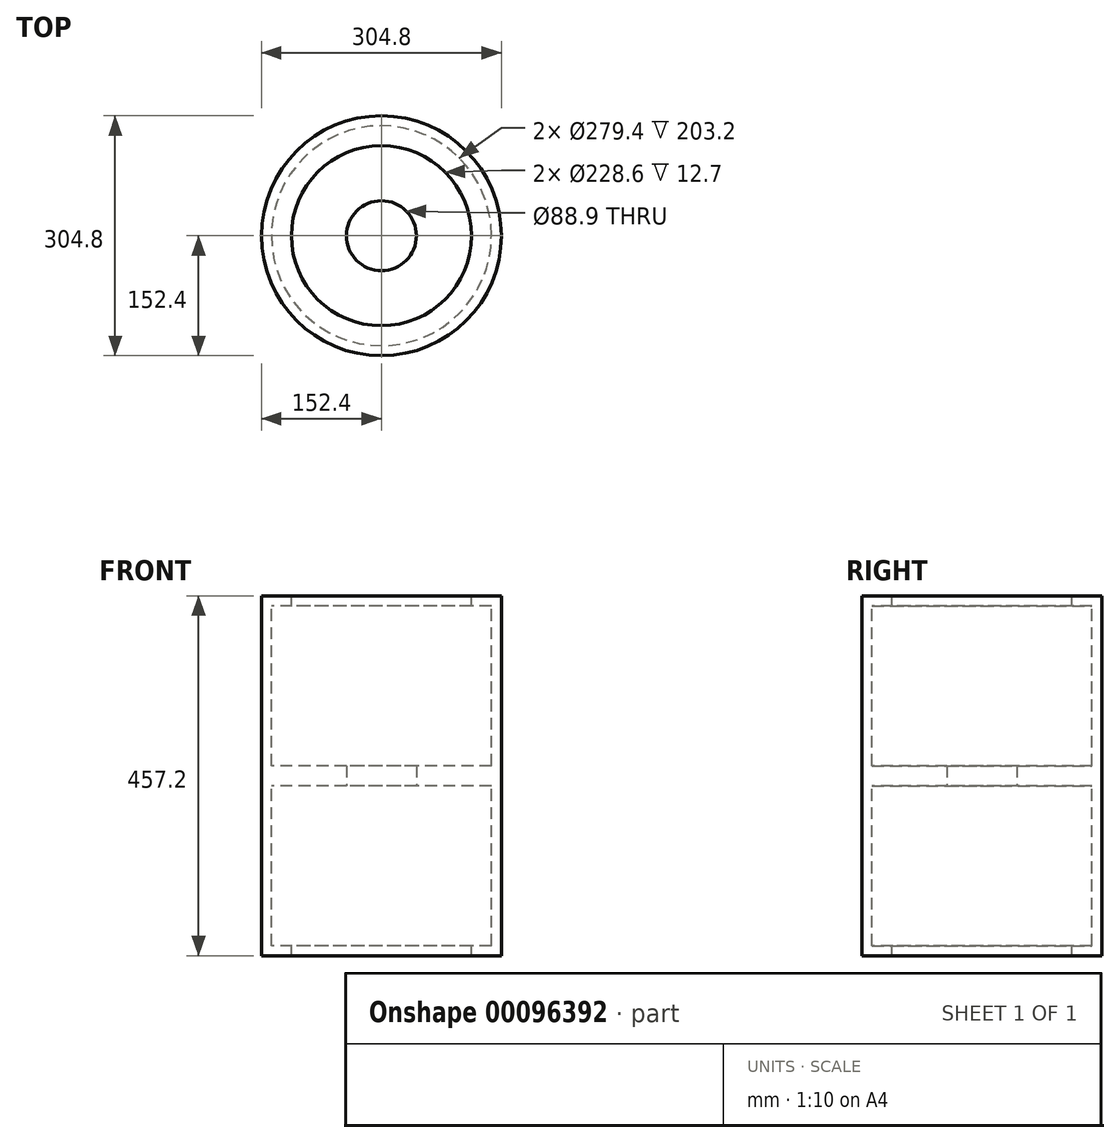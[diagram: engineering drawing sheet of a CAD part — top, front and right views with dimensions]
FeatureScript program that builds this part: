
annotation { "Feature Type Name" : "Feature", "Feature Type Description" : "" }
export const myFeature = defineFeature(function(context is Context, id is Id, definition is map)
    precondition{}
    {
        {
            var Q0;
            Q0=qCreatedBy(makeId("Front.planeOp"),FACE);
            var sketch = newSketch(context, id + "F0", { "sketchPlane" : qUnion([Q0])});
            skLineSegment(sketch, "E0.bottom", {"start": v(152.4, 228.6) * mm, "end": v(-152.4, 228.6) * mm});
            skLineSegment(sketch, "E0.top", {"start": v(152.4, -228.6) * mm, "end": v(-152.4, -228.6) * mm});
            skLineSegment(sketch, "E0.left", {"start": v(152.4, 228.6) * mm, "end": v(152.4, -228.6) * mm});
            skLineSegment(sketch, "E0.right", {"start": v(-152.4, 228.6) * mm, "end": v(-152.4, -228.6) * mm});
            skPoint(sketch, "E0.middle", {"position": v(0, 0) * mm});
            skLineSegment(sketch, "E1", {"start": v(0, 228.6) * mm, "end": v(0, -228.6) * mm});
            skLineSegment(sketch, "E2.bottom", {"start": v(114.3, 228.6) * mm, "end": v(-114.3, 228.6) * mm});
            skLineSegment(sketch, "E2.top", {"start": v(114.3, -228.6) * mm, "end": v(-114.3, -228.6) * mm});
            skLineSegment(sketch, "E2.left", {"start": v(114.3, 228.6) * mm, "end": v(114.3, -228.6) * mm});
            skLineSegment(sketch, "E2.right", {"start": v(-114.3, 228.6) * mm, "end": v(-114.3, -228.6) * mm});
            skLineSegment(sketch, "E3.bottom", {"start": v(-114.3, 215.9) * mm, "end": v(-139.7, 215.9) * mm});
            skLineSegment(sketch, "E3.top", {"start": v(-114.3, -215.9) * mm, "end": v(-139.7, -215.9) * mm});
            skLineSegment(sketch, "E3.left", {"start": v(-114.3, 215.9) * mm, "end": v(-114.3, -215.9) * mm});
            skLineSegment(sketch, "E3.right", {"start": v(-139.7, 215.9) * mm, "end": v(-139.7, -215.9) * mm});
            skLineSegment(sketch, "E4.bottom", {"start": v(114.3, 210.5) * mm, "end": v(139.7, 210.5) * mm});
            skLineSegment(sketch, "E4.top", {"start": v(114.3, -212.35) * mm, "end": v(139.7, -212.35) * mm});
            skLineSegment(sketch, "E4.left", {"start": v(114.3, 210.5) * mm, "end": v(114.3, -212.35) * mm});
            skLineSegment(sketch, "E4.right", {"start": v(139.7, 210.5) * mm, "end": v(139.7, -212.35) * mm});
            skSolve(sketch);
        }
        {
            var Q0;
            {var subQ5=sQuery(id+"F0.wireOp",EDGE,"E0.right");Q0=makeQuery(id+"F0.imprint","IMPRINT",FACE,{"disambiguationData":[TD([[makeQuery(id+"F0.imprint","IMPRINT",EDGE,{"derivedFrom":subQ5}),1.0]])]});}
            var Q1;
            Q1=sQuery(id+"F0.wireOp",EDGE,"E1");
            revolve(context, id + "F1", {"entities" : qUnion([Q0]), "axis" : qUnion([Q1]), "revolveType" : RevolveType.FULL});
        }
        {
            var Q0;
            Q0=qCreatedBy(makeId("Top.planeOp"),FACE);
            var sketch = newSketch(context, id + "F2", { "sketchPlane" : qUnion([Q0])});
            skCircle(sketch, "E5", {"center": v(0, 0) * mm, "radius": 152.4 * mm});
            skCircle(sketch, "E6", {"center": v(0, 0) * mm, "radius": 44.45 * mm});
            skSolve(sketch);
        }
        {
            var Q0;
            Q0 = qSketchRegion(id + "F2", true);
            extrude(context, id + "F3", {"entities" : qUnion([Q0]), "operationType" : NewBodyOperationType.ADD, "endBound" : BoundingType.SYMMETRIC, "depth" : 12.7 * mm});
        }
        {
            var Q0;
            Q0 = qSketchRegion(id + "F2", true);
            extrude(context, id + "F4", {"entities" : qUnion([Q0]), "operationType" : NewBodyOperationType.ADD, "endBound" : BoundingType.SYMMETRIC, "depth" : 25.4 * mm});
        }
    });
